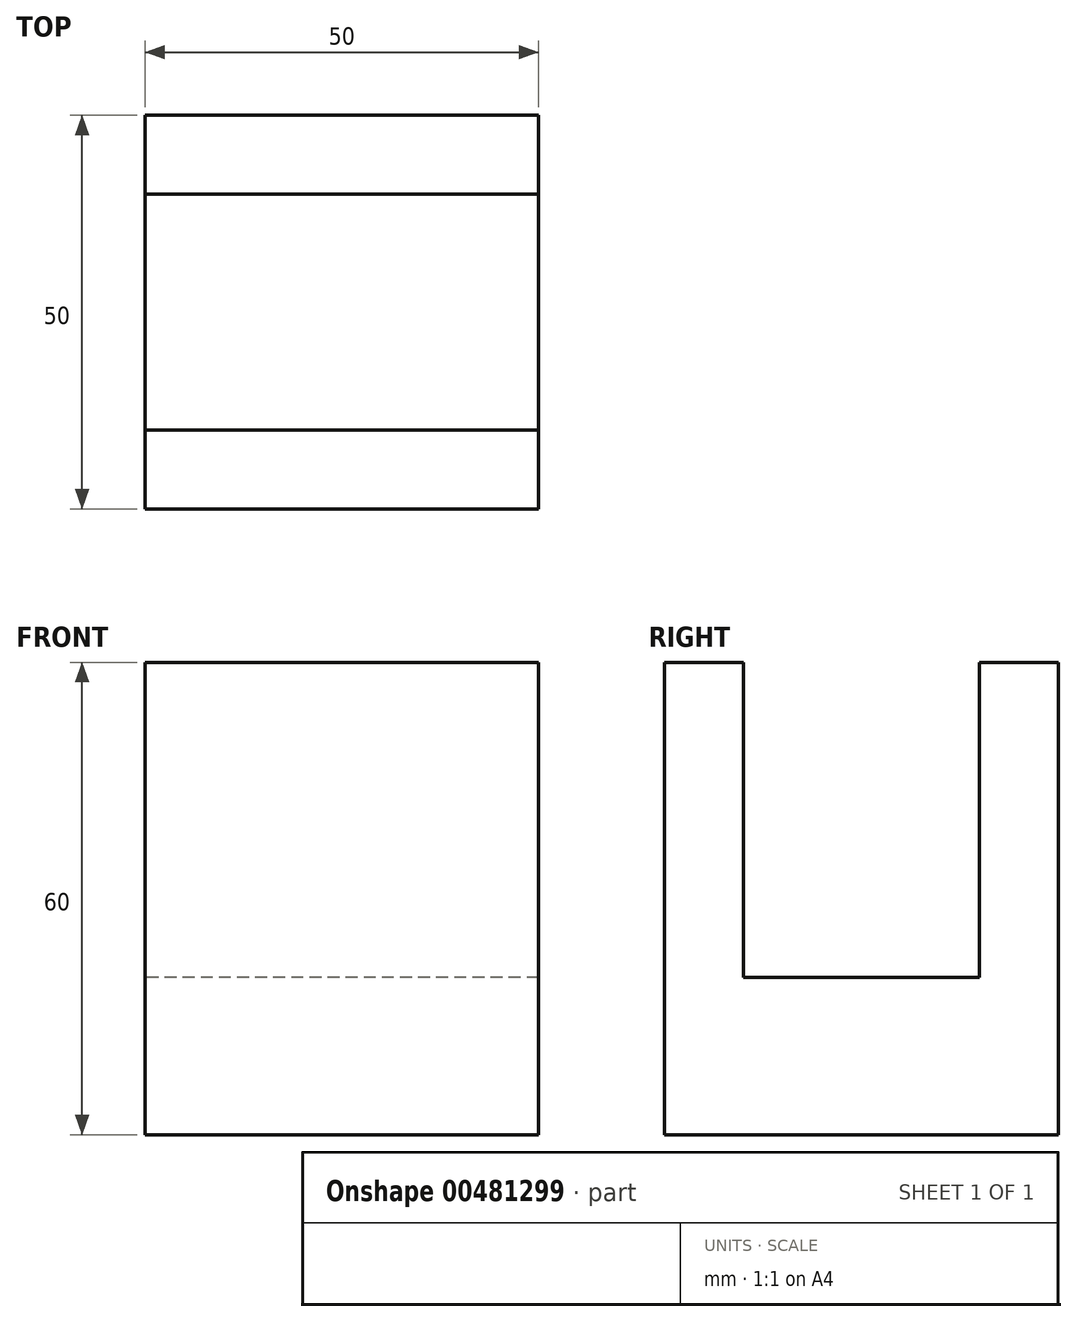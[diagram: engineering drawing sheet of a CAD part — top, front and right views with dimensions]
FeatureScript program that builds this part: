
annotation { "Feature Type Name" : "Feature", "Feature Type Description" : "" }
export const myFeature = defineFeature(function(context is Context, id is Id, definition is map)
    precondition{}
    {
        {
            var Q0;
            Q0=qCreatedBy(makeId("Right.planeOp"),FACE);
            var sketch = newSketch(context, id + "F0", { "sketchPlane" : qUnion([Q0])});
            skLineSegment(sketch, "E0", {"start": v(0, 0) * mm, "end": v(0, 60) * mm});
            skLineSegment(sketch, "E1", {"start": v(0, 60) * mm, "end": v(10, 60) * mm});
            skLineSegment(sketch, "E2", {"start": v(10, 60) * mm, "end": v(10, 20) * mm});
            skLineSegment(sketch, "E3", {"start": v(10, 20) * mm, "end": v(40, 20) * mm});
            skLineSegment(sketch, "E4", {"start": v(40, 20) * mm, "end": v(40, 60) * mm});
            skLineSegment(sketch, "E5", {"start": v(40, 60) * mm, "end": v(50, 60) * mm});
            skLineSegment(sketch, "E6", {"start": v(50, 60) * mm, "end": v(50, 0) * mm});
            skLineSegment(sketch, "E7", {"start": v(50, 0) * mm, "end": v(0, 0) * mm});
            skSolve(sketch);
        }
        {
            var Q0;
            Q0=makeQuery(id+"F0.imprint","IMPRINT",FACE,{"disambiguationData":[TD([[makeQuery(id+"F0.imprint","IMPRINT",EDGE,{"derivedFrom":sQuery(id+"F0.wireOp",EDGE,"E0")}),-1.0]])]});
            extrude(context, id + "F1", {"entities" : qUnion([Q0]), "depth" : 50 * mm});
        }
    });
